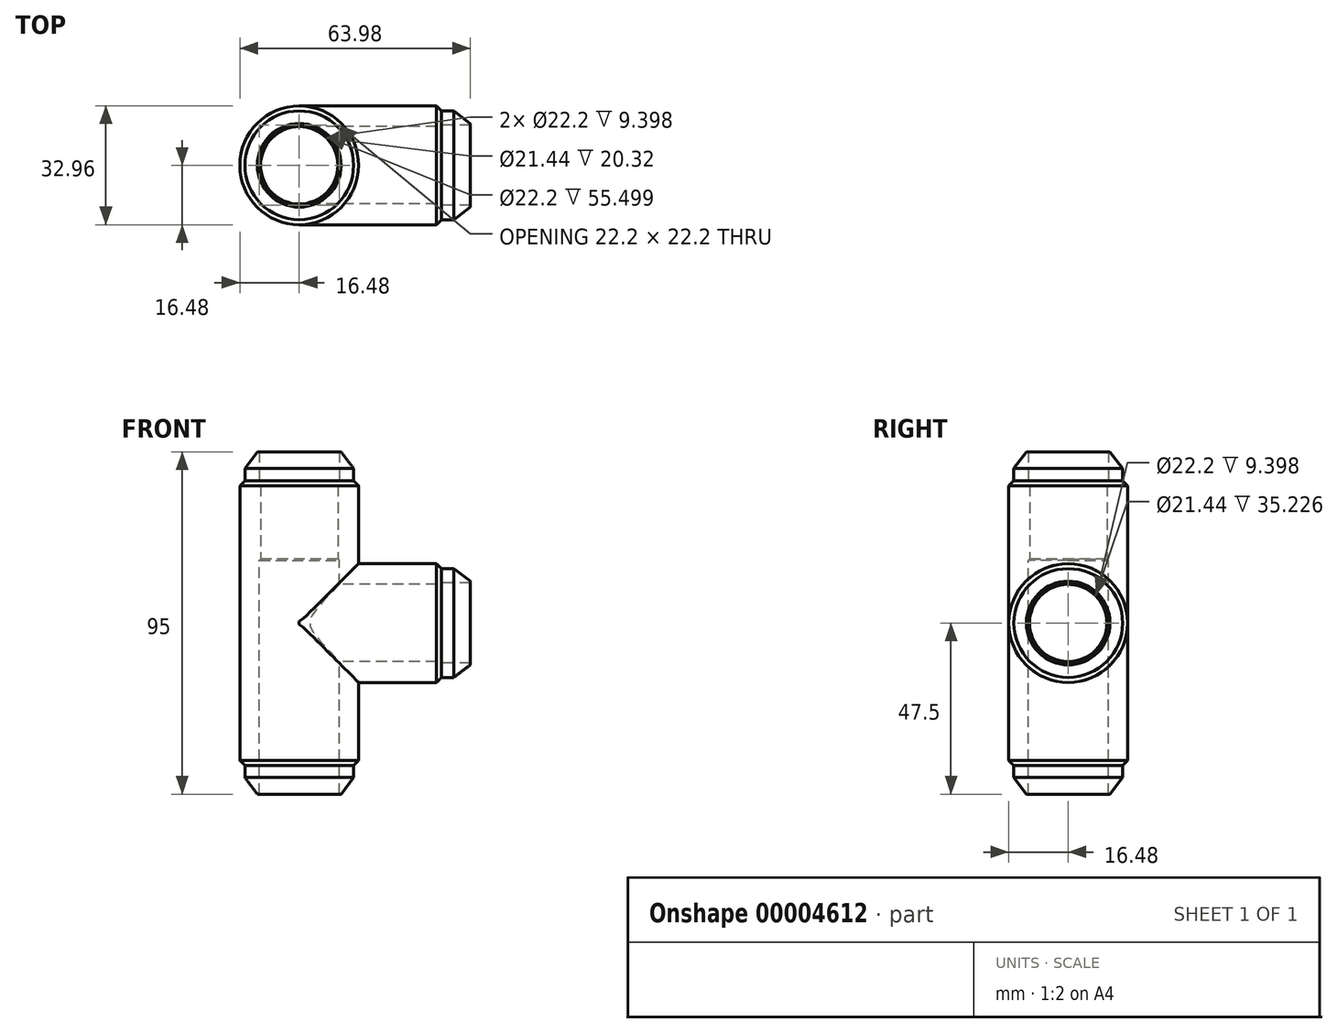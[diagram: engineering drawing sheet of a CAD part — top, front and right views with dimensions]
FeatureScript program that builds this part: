
annotation { "Feature Type Name" : "Feature", "Feature Type Description" : "" }
export const myFeature = defineFeature(function(context is Context, id is Id, definition is map)
    precondition{}
    {
        {
            var Q0;
            Q0=qCreatedBy(makeId("Top.planeOp"),FACE);
            var sketch = newSketch(context, id + "F0", { "sketchPlane" : qUnion([Q0])});
            skCircle(sketch, "E0", {"center": v(0, 0) * mm, "radius": 10.72 * mm});
            skCircle(sketch, "E1", {"center": v(0, 0) * mm, "radius": 16.48 * mm});
            skSolve(sketch);
        }
        {
            var Q0;
            Q0 = qSketchRegion(id + "F0", true);
            extrude(context, id + "F1", {"entities" : qUnion([Q0]), "endBound" : BoundingType.SYMMETRIC, "depth" : 76.2 * mm});
        }
        {
            var Q0;
            Q0=qCreatedBy(makeId("Right.planeOp"),FACE);
            var sketch = newSketch(context, id + "F2", { "sketchPlane" : qUnion([Q0])});
            skCircle(sketch, "E2", {"center": v(0, 0) * mm, "radius": 16.48 * mm});
            skCircle(sketch, "E3", {"center": v(0, 0) * mm, "radius": 10.72 * mm});
            skSolve(sketch);
        }
        {
            var Q0;
            Q0 = qSketchRegion(id + "F2", true);
            extrude(context, id + "F3", {"entities" : qUnion([Q0]), "operationType" : NewBodyOperationType.ADD, "depth" : 38.1 * mm});
        }
        {
            var Q0;
            Q0=qCreatedBy(makeId("Top.planeOp"),FACE);
            var sketch = newSketch(context, id + "F4", { "sketchPlane" : qUnion([Q0])});
            skCircle(sketch, "E4", {"center": v(0, 0) * mm, "radius": 10.72 * mm});
            skSolve(sketch);
        }
        {
            var Q0;
            Q0 = qSketchRegion(id + "F4", true);
            extrude(context, id + "F5", {"entities" : qUnion([Q0]), "operationType" : NewBodyOperationType.REMOVE, "endBound" : BoundingType.SYMMETRIC, "oppositeDirection" : true, "depth" : 254 * mm});
        }
        {
            var Q0;
            Q0=qCreatedBy(makeId("Right.planeOp"),FACE);
            var sketch = newSketch(context, id + "F6", { "sketchPlane" : qUnion([Q0])});
            skCircle(sketch, "E5", {"center": v(0, 0) * mm, "radius": 10.72 * mm});
            skSolve(sketch);
        }
        {
            var Q0;
            Q0 = qSketchRegion(id + "F6", true);
            extrude(context, id + "F7", {"entities" : qUnion([Q0]), "operationType" : NewBodyOperationType.REMOVE, "endBound" : BoundingType.THROUGH_ALL, "depth" : 25.4 * mm});
        }
        {
            var Q0;
            Q0=qCreatedBy(makeId("Top.planeOp"),FACE);
            cPlane(context, id + "F8", {"entities" : qUnion([Q0]), "cplaneType" : CPlaneType.OFFSET, "offset" : 15.24 * mm, "width" : 152.4 * mm, "height" : 152.4 * mm});
        }
        {
            var Q0;
            Q0=qCreatedBy(makeId("Right.planeOp"),FACE);
            var sketch = newSketch(context, id + "F9", { "sketchPlane" : qUnion([Q0])});
            skLineSegment(sketch, "E6", {"start": v(16.48, -38.1) * mm, "end": v(15.09, -39.5) * mm});
            skLineSegment(sketch, "E7", {"start": v(15.09, -39.5) * mm, "end": v(15.09, -42.86) * mm});
            skLineSegment(sketch, "E8", {"start": v(15.09, -42.86) * mm, "end": v(11.6, -47.5) * mm});
            skLineSegment(sketch, "E9", {"start": v(11.6, -47.5) * mm, "end": v(10.72, -47.5) * mm});
            skLineSegment(sketch, "E10", {"start": v(10.72, -47.5) * mm, "end": v(10.72, -38.1) * mm});
            skLineSegment(sketch, "E11", {"start": v(10.72, -38.1) * mm, "end": v(16.48, -38.1) * mm});
            skSolve(sketch);
        }
        {
            var Q0;
            Q0 = qSketchRegion(id + "F9", true);
            var Q1;
            {var subQ0=sQuery(id+"F0.wireOp",EDGE,"E0");var subQ1=makeQuery(id+"F1.opExtrude","SWEPT_FACE",FACE,{"disambiguationData":[OSD([subQ0])]});var subQ2=sQuery(id+"F2.wireOp",EDGE,"E3");var subQ3=makeQuery(id+"F3.opExtrude","SWEPT_FACE",FACE,{"disambiguationData":[OSD([subQ2])]});var subQ4=sQuery(id+"F2.wireOp",EDGE,"E2");var subQ5=makeQuery(id+"F3.opExtrude","CAP_FACE",FACE,{"disambiguationData":[OSD([subQ4,subQ2])],"isStart":true});var subQ6=sQuery(id+"F0.wireOp",EDGE,"E1");Q1=makeQuery(id+"F5.boolean.opBoolean","MERGE",FACE,{"derivedFrom":[makeQuery(id+"F3.boolean.opBoolean","SPLIT",FACE,{"disambiguationData":[TD([subQ1,subQ5,subQ3])],"derivedFrom":subQ1}),makeQuery(id+"F3.boolean.opBoolean","SPLIT",FACE,{"disambiguationData":[TD([subQ1,makeQuery(id+"F1.opExtrude","CAP_FACE",FACE,{"disambiguationData":[OSD([subQ0,subQ6])],"isStart":true}),makeQuery(id+"F1.opExtrude","CAP_FACE",FACE,{"disambiguationData":[OSD([subQ0,subQ6])],"isStart":false}),makeQuery(id+"F3.opExtrude","SWEPT_FACE",FACE,{"disambiguationData":[OSD([subQ4])]}),subQ5,subQ3])],"derivedFrom":subQ1}),makeQuery(id+"F5.opExtrude","SWEPT_FACE",FACE,{"disambiguationData":[OSD([sQuery(id+"F4.wireOp",EDGE,"E4")])]})]});}
            revolve(context, id + "F10", {"entities" : qUnion([Q0]), "axis" : qUnion([Q1]), "revolveType" : RevolveType.FULL});
        }
        {
            var Q0;
            Q0=qCreatedBy(id+"F8.planeOp",FACE);
            var sketch = newSketch(context, id + "F11", { "sketchPlane" : qUnion([Q0])});
            skCircle(sketch, "E12", {"center": v(0, 0) * mm, "radius": 11.1 * mm});
            skSolve(sketch);
        }
        {
            var Q0;
            Q0 = qSketchRegion(id + "F11", true);
            extrude(context, id + "F12", {"entities" : qUnion([Q0]), "operationType" : NewBodyOperationType.REMOVE, "endBound" : BoundingType.THROUGH_ALL, "oppositeDirection" : true, "depth" : 25.4 * mm});
        }
        {
            var Q0;
            Q0=qCreatedBy(makeId("Top.planeOp"),FACE);
            var sketch = newSketch(context, id + "F13", { "sketchPlane" : qUnion([Q0])});
            skLineSegment(sketch, "E13", {"start": v(0, 0) * mm, "end": v(0, -27.79) * mm});
            skSolve(sketch);
        }
        {
            var Q0;
            Q0=makeQuery(id+"F10.opRevolve","SWEPT_BODY",BODY,{"disambiguationData":[OSD([sQuery(id+"F9.wireOp",EDGE,"E6"),sQuery(id+"F9.wireOp",EDGE,"E7"),sQuery(id+"F9.wireOp",EDGE,"E8"),sQuery(id+"F9.wireOp",EDGE,"E9"),sQuery(id+"F9.wireOp",EDGE,"E10"),sQuery(id+"F9.wireOp",EDGE,"E11")])]});
            var Q1;
            Q1=sQuery(id+"F13.wireOp",EDGE,"E13");
            circularPattern(context, id + "F14", {"entities" : qUnion([Q0]), "axis" : qUnion([Q1]), "angle" : 90 * degree, "instanceCount" : 3});
        }
        {
            var Q0;
            {var subQ0=sQuery(id+"F0.wireOp",EDGE,"E0");var subQ1=makeQuery(id+"F1.opExtrude","SWEPT_FACE",FACE,{"disambiguationData":[OSD([subQ0])]});var subQ2=sQuery(id+"F2.wireOp",EDGE,"E3");var subQ3=makeQuery(id+"F3.opExtrude","SWEPT_FACE",FACE,{"disambiguationData":[OSD([subQ2])]});var subQ4=sQuery(id+"F2.wireOp",EDGE,"E2");var subQ5=makeQuery(id+"F3.opExtrude","CAP_FACE",FACE,{"disambiguationData":[OSD([subQ4,subQ2])],"isStart":true});var subQ6=sQuery(id+"F0.wireOp",EDGE,"E1");Q0=makeQuery(id+"F12.boolean.opBoolean","INTERSECT",EDGE,{"derivedFrom":[makeQuery(id+"F5.boolean.opBoolean","MERGE",FACE,{"derivedFrom":[makeQuery(id+"F3.boolean.opBoolean","SPLIT",FACE,{"disambiguationData":[TD([subQ1,subQ5,subQ3])],"derivedFrom":subQ1}),makeQuery(id+"F3.boolean.opBoolean","SPLIT",FACE,{"disambiguationData":[TD([subQ1,makeQuery(id+"F1.opExtrude","CAP_FACE",FACE,{"disambiguationData":[OSD([subQ0,subQ6])],"isStart":true}),makeQuery(id+"F1.opExtrude","CAP_FACE",FACE,{"disambiguationData":[OSD([subQ0,subQ6])],"isStart":false}),makeQuery(id+"F3.opExtrude","SWEPT_FACE",FACE,{"disambiguationData":[OSD([subQ4])]}),subQ5,subQ3])],"derivedFrom":subQ1}),makeQuery(id+"F5.opExtrude","SWEPT_FACE",FACE,{"disambiguationData":[OSD([sQuery(id+"F4.wireOp",EDGE,"E4")])]})]}),makeQuery(id+"F12.opExtrude","CAP_FACE",FACE,{"disambiguationData":[OSD([sQuery(id+"F11.wireOp",EDGE,"E12")])],"isStart":true})]});}
            chamfer(context, id + "F15", {"entities" : qUnion([Q0]), "width" : 2.54 * mm, "tangentPropagation" : true});
        }
    });
